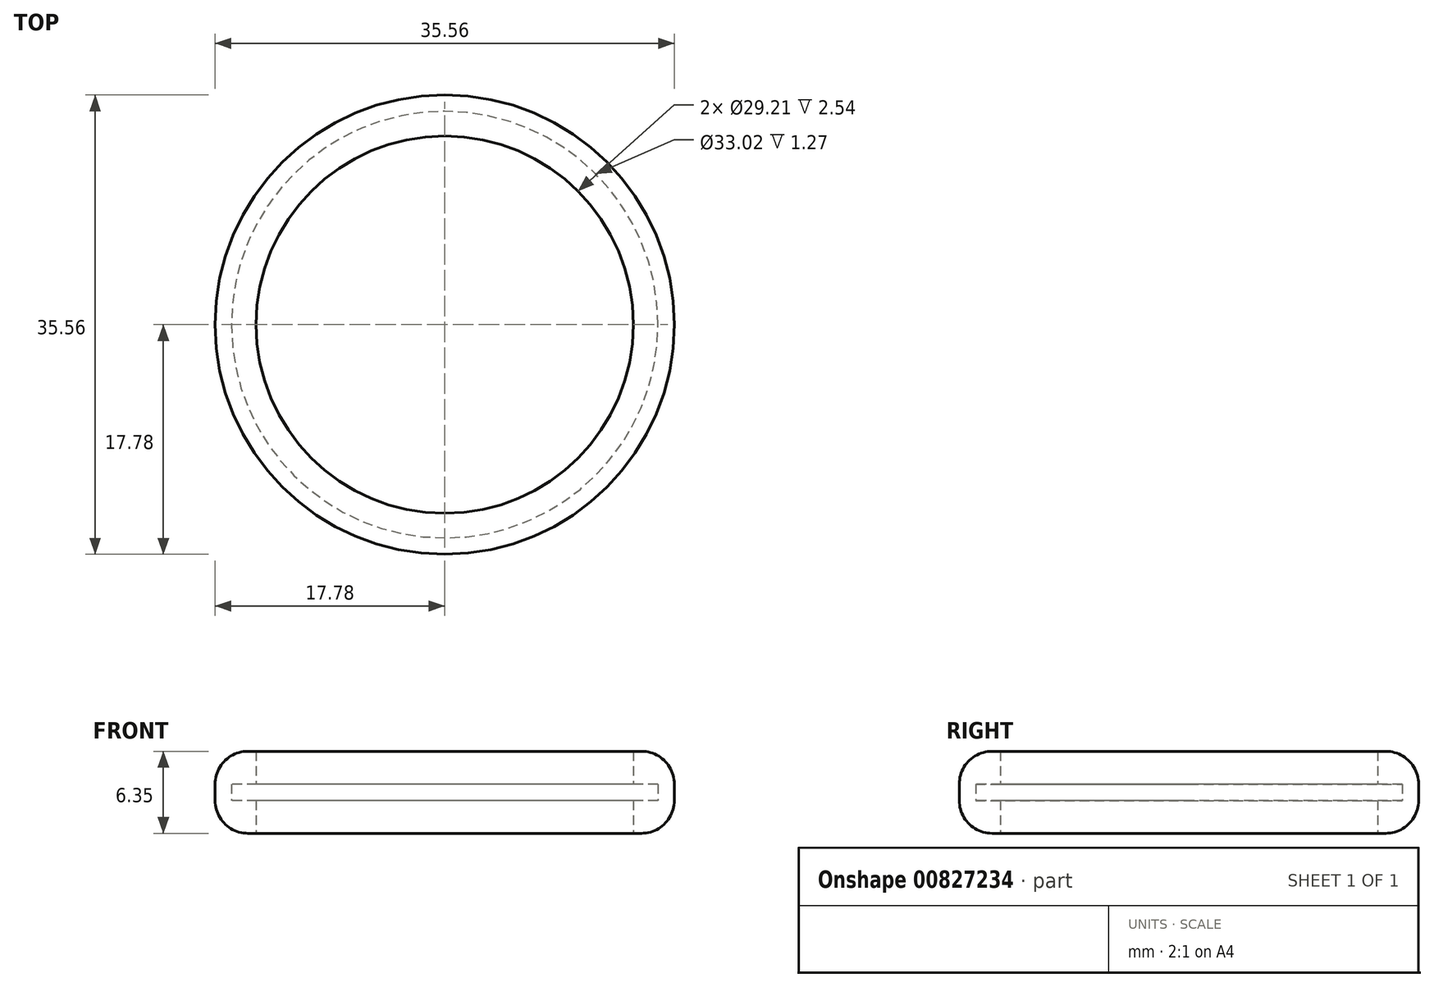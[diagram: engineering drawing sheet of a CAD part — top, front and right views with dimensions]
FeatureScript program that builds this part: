
annotation { "Feature Type Name" : "Feature", "Feature Type Description" : "" }
export const myFeature = defineFeature(function(context is Context, id is Id, definition is map)
    precondition{}
    {
        {
            var Q0;
            Q0=qCreatedBy(makeId("Top.planeOp"),FACE);
            var sketch = newSketch(context, id + "F0", { "sketchPlane" : qUnion([Q0])});
            skCircle(sketch, "E0", {"center": v(0, 0) * mm, "radius": 17.78 * mm});
            skSolve(sketch);
        }
        {
            var Q0;
            Q0=makeQuery(id+"F0.imprint","IMPRINT",FACE,{"disambiguationData":[TD([[makeQuery(id+"F0.imprint","IMPRINT",EDGE,{"derivedFrom":sQuery(id+"F0.wireOp",EDGE,"E0")}),1.0]])]});
            extrude(context, id + "F1", {"entities" : qUnion([Q0]), "depth" : 2.54 * mm, "offsetDistance" : 25.4 * mm});
        }
        {
            var Q0;
            Q0=makeQuery(id+"F1.opExtrude","CAP_FACE",FACE,{"disambiguationData":[OSD([sQuery(id+"F0.wireOp",EDGE,"E0")])],"isStart":false});
            var sketch = newSketch(context, id + "F2", { "sketchPlane" : qUnion([Q0])});
            skCircle(sketch, "E1", {"center": v(0, 0) * mm, "radius": 17.78 * mm});
            skCircle(sketch, "E2", {"center": v(0, 0) * mm, "radius": 16.51 * mm});
            skSolve(sketch);
        }
        {
            var Q0;
            Q0=makeQuery(id+"F2.imprint","IMPRINT",FACE,{"disambiguationData":[TD([[makeQuery(id+"F2.imprint","IMPRINT",EDGE,{"derivedFrom":sQuery(id+"F2.wireOp",EDGE,"E2")}),-1.0]])]});
            extrude(context, id + "F3", {"entities" : qUnion([Q0]), "operationType" : NewBodyOperationType.ADD, "depth" : 1.27 * mm, "offsetDistance" : 25.4 * mm});
        }
        {
            var Q0;
            Q0=makeQuery(id+"F3.opExtrude","CAP_FACE",FACE,{"disambiguationData":[OSD([sQuery(id+"F0.wireOp",EDGE,"E0"),sQuery(id+"F2.wireOp",EDGE,"E2")])],"isStart":false});
            var sketch = newSketch(context, id + "F4", { "sketchPlane" : qUnion([Q0])});
            skCircle(sketch, "E3", {"center": v(0, 0) * mm, "radius": 17.78 * mm});
            skSolve(sketch);
        }
        {
            var Q0;
            Q0 = qSketchRegion(id + "F4", true);
            extrude(context, id + "F5", {"entities" : qUnion([Q0]), "operationType" : NewBodyOperationType.ADD, "depth" : 2.54 * mm, "offsetDistance" : 25.4 * mm});
        }
        {
            var Q0;
            Q0=makeQuery(id+"F1.opExtrude","CAP_FACE",FACE,{"disambiguationData":[OSD([sQuery(id+"F0.wireOp",EDGE,"E0")])],"isStart":true});
            var sketch = newSketch(context, id + "F6", { "sketchPlane" : qUnion([Q0])});
            skCircle(sketch, "E4", {"center": v(0, 0) * mm, "radius": 14.6 * mm});
            skSolve(sketch);
        }
        {
            var Q0;
            Q0=makeQuery(id+"F6.imprint","IMPRINT",FACE,{"disambiguationData":[TD([[makeQuery(id+"F6.imprint","IMPRINT",EDGE,{"derivedFrom":sQuery(id+"F6.wireOp",EDGE,"E4")}),1.0]])]});
            extrude(context, id + "F7", {"entities" : qUnion([Q0]), "operationType" : NewBodyOperationType.REMOVE, "oppositeDirection" : true, "depth" : 50.8 * mm, "offsetDistance" : 25.4 * mm});
        }
        {
            var Q0;
            Q0=makeQuery(id+"F5.opExtrude","CAP_EDGE",EDGE,{"disambiguationData":[OSD([sQuery(id+"F4.wireOp",EDGE,"E3")])],"isStart":false});
            var Q1;
            Q1=makeQuery(id+"F1.opExtrude","CAP_EDGE",EDGE,{"disambiguationData":[OSD([sQuery(id+"F0.wireOp",EDGE,"E0")])],"isStart":true});
            fillet(context, id + "F8", {"entities" : qUnion([Q0, Q1]), "radius" : 2.54 * mm, "tangentPropagation" : true, "allowEdgeOverflow" : false});
        }
    });
